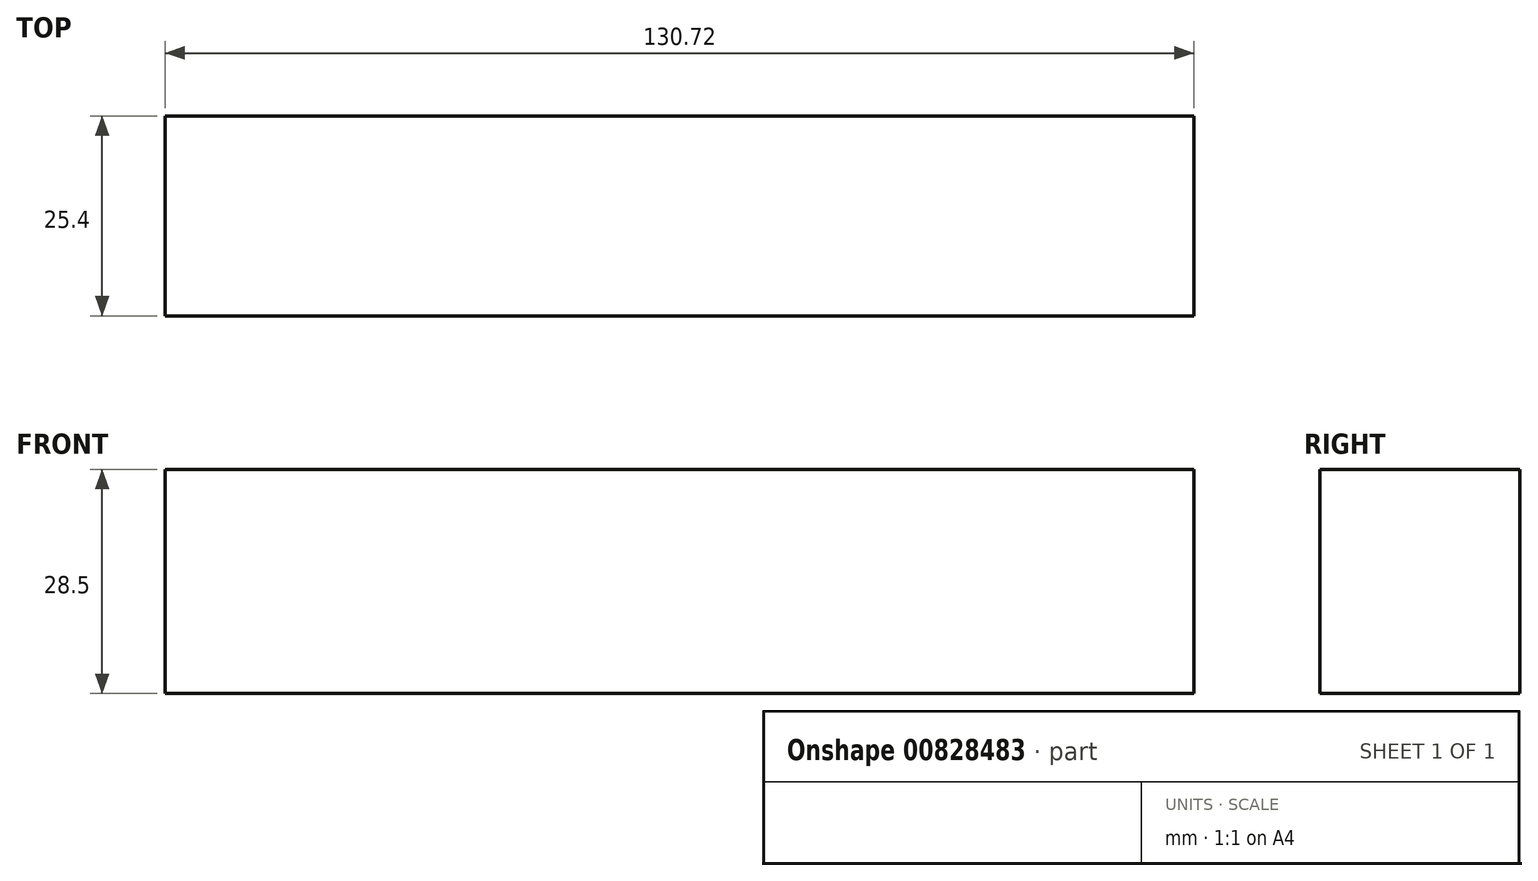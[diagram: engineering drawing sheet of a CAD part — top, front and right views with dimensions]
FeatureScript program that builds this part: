
annotation { "Feature Type Name" : "Feature", "Feature Type Description" : "" }
export const myFeature = defineFeature(function(context is Context, id is Id, definition is map)
    precondition{}
    {
        {
            var Q0;
            Q0=qCreatedBy(makeId("Front.planeOp"),FACE);
            var sketch = newSketch(context, id + "F0", { "sketchPlane" : qUnion([Q0])});
            skLineSegment(sketch, "E0.bottom", {"start": v(-65.36, 14.25) * mm, "end": v(65.36, 14.25) * mm});
            skLineSegment(sketch, "E0.top", {"start": v(-65.36, -14.25) * mm, "end": v(65.36, -14.25) * mm});
            skLineSegment(sketch, "E0.left", {"start": v(-65.36, 14.25) * mm, "end": v(-65.36, -14.25) * mm});
            skLineSegment(sketch, "E0.right", {"start": v(65.36, 14.25) * mm, "end": v(65.36, -14.25) * mm});
            skPoint(sketch, "E0.middle", {"position": v(0, 0) * mm});
            skSolve(sketch);
        }
        {
            var Q0;
            Q0=makeQuery(id+"F0.imprint","IMPRINT",FACE,{"disambiguationData":[TD([[makeQuery(id+"F0.imprint","IMPRINT",EDGE,{"derivedFrom":sQuery(id+"F0.wireOp",EDGE,"E0.bottom")}),-1.0]])]});
            extrude(context, id + "F1", {"entities" : qUnion([Q0]), "endBound" : BoundingType.SYMMETRIC, "depth" : 25.4 * mm, "offsetDistance" : 25.4 * mm});
        }
    });
